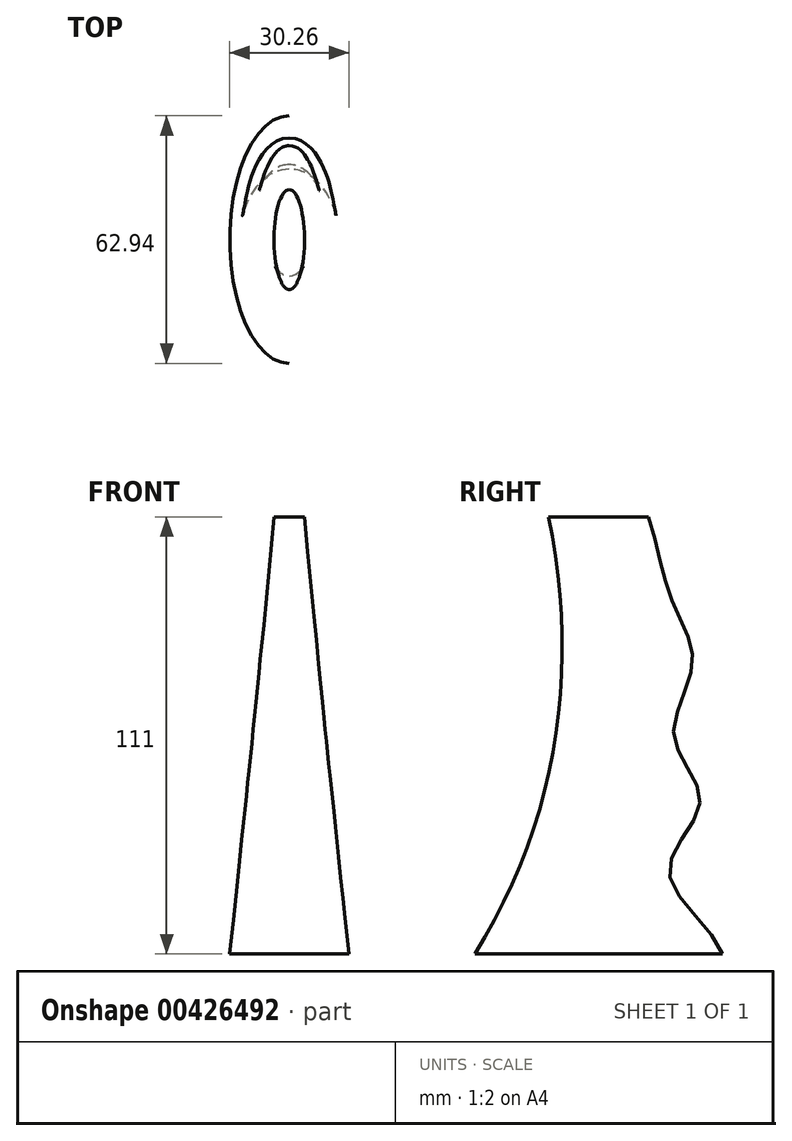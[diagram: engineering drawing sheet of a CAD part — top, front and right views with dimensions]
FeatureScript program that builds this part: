
annotation { "Feature Type Name" : "Feature", "Feature Type Description" : "" }
export const myFeature = defineFeature(function(context is Context, id is Id, definition is map)
    precondition{}
    {
        {
            var Q0;
            Q0=qCreatedBy(makeId("Top.planeOp"),FACE);
            var sketch = newSketch(context, id + "F0", { "sketchPlane" : qUnion([Q0])});
            skEllipse(sketch, "E0", {"center": v(0, 0) * mm, "majorRadius": 31.47 * mm, "minorRadius": 15.13 * mm, "majorAxis": v(0, 1)});
            skPoint(sketch, "E1", {"position": v(0, 31.47) * mm});
            skPoint(sketch, "E2", {"position": v(0, -31.47) * mm});
            skSolve(sketch);
        }
        {
            var Q0;
            Q0=qCreatedBy(makeId("Top.planeOp"),FACE);
            cPlane(context, id + "F1", {"entities" : qUnion([Q0]), "cplaneType" : CPlaneType.OFFSET, "offset" : 111 * mm, "width" : 152.4 * mm, "height" : 152.4 * mm});
        }
        {
            var Q0;
            Q0=qCreatedBy(id+"F1.planeOp",FACE);
            var sketch = newSketch(context, id + "F2", { "sketchPlane" : qUnion([Q0])});
            skEllipse(sketch, "E3", {"center": v(0, 0) * mm, "majorRadius": 12.7 * mm, "minorRadius": 3.87 * mm, "majorAxis": v(0, 1)});
            skPoint(sketch, "E4", {"position": v(0, 12.7) * mm});
            skPoint(sketch, "E5", {"position": v(0, -12.7) * mm});
            skSolve(sketch);
        }
        {
            var Q0;
            Q0=qCreatedBy(makeId("Right.planeOp"),FACE);
            var sketch = newSketch(context, id + "F3", { "sketchPlane" : qUnion([Q0])});
            skFitSpline(sketch, "E6", {"points": [v(31.47, 0) * mm, v(17.9, 20.77) * mm, v(25.82, 38.6) * mm, v(19.15, 54.9) * mm, v(23.85, 73.56) * mm, v(18.69, 89.56) * mm, v(12.7, 111) * mm], "startDerivative": vector(-36.61, 108.75) * mm, "endDerivative": vector(-40.77, 128.91) * mm});
            skFitSpline(sketch, "E7", {"points": [v(-31.47, 0) * mm, v(-12.7, 111) * mm], "startDerivative": vector(61.72, 99) * mm, "endDerivative": vector(-24.47, 121.24) * mm});
            skSolve(sketch);
        }
        {
            var Q0;
            Q0=makeQuery(id+"F0.imprint","IMPRINT",FACE,{"disambiguationData":[TD([[makeQuery(id+"F0.imprint","IMPRINT",EDGE,{"derivedFrom":sQuery(id+"F0.wireOp",EDGE,"E0")}),1.0]])]});
            var Q1;
            Q1=makeQuery(id+"F2.imprint","IMPRINT",FACE,{"disambiguationData":[TD([[makeQuery(id+"F2.imprint","IMPRINT",EDGE,{"derivedFrom":sQuery(id+"F2.wireOp",EDGE,"E3")}),1.0]])]});
            var Q2;
            Q2=sQuery(id+"F3.wireOp",EDGE,"E6");
            var Q3;
            Q3=sQuery(id+"F3.wireOp",EDGE,"E7");
            loft(context, id + "F4", {"addGuides" : true, "sheetProfilesArray" : [{ "sheetProfileEntities" : qUnion([Q0]) }, { "sheetProfileEntities" : qUnion([Q1]) }], "guidesArray" : [{ "guideEntities" : qUnion([Q2]), "guideDerivativeType" : LoftGuideDerivativeType.DEFAULT, "guideDerivativeMagnitude" : 1 }, { "guideEntities" : qUnion([Q3]), "guideDerivativeType" : LoftGuideDerivativeType.DEFAULT, "guideDerivativeMagnitude" : 1 }]});
        }
    });
